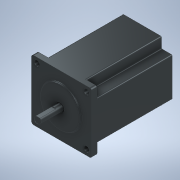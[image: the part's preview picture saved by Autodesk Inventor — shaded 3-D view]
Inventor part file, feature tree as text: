
AUTODESK INVENTOR PART (.ipt)
format: ipt  version: 2020 (Build 240168000, 168)  size: 250,368 bytes
history: native  units: mm
features: extrude x6, sketch x6, fillet x2, projected_geometry x2
ambient origin geometry x8: Origin, YZ Plane, XZ Plane, XY Plane, X Axis, Y Axis, Z Axis, Center Point
bodies: Body1 (feature_tree)
feature tree (16):
  extrude  "Extrusion4"  Depth=57.3mm
  extrude  "Extrusion5"  Depth=10.16mm
  fillet  "Fillet1"  Radius=10.16mm
  extrude  "Extrusion6"  Depth=1.0mm
  extrude  "Extrusion7"  Depth=76.5mm
  extrude  "Extrusion8"  Depth=5.08mm
  extrude  "Extrusion9"  Depth=0.5mm
  fillet  "Fillet2"  Radius=5.2mm
  sketch  "Sketch1"  dims[d25=57.3mm d26=57.3mm]
  sketch  "Sketch4"  dims[d27=10.16mm d28=10.16mm d29=10.16mm]
  projected_geometry  "Projected Loop2"
  sketch  "Sketch5"  dims[d30=10.16mm d31=1.0mm]
  projected_geometry  "Projected Loop3"
  sketch  "Sketch6"  dims[d32=76.5mm d33=0.0mm d34=5.08mm]
  sketch  "Sketch7"  dims[d35=5.08mm d36=5.08mm]
  sketch  "Sketch8"  dims[d37=5.08mm d38=5.2mm d39=5.2mm d40=5.2mm d41=5.2mm d42=5.0mm d43=0.0mm d44=2.0mm d45=38.1mm d46=1.6mm d47=0.0mm d48=6.35mm d49=6.0mm d50=0.0mm d51=2.5mm d52=15.0mm d53=0.0mm d54=8.0mm d55=2.0mm d56=0.0mm d57=0.5mm]
